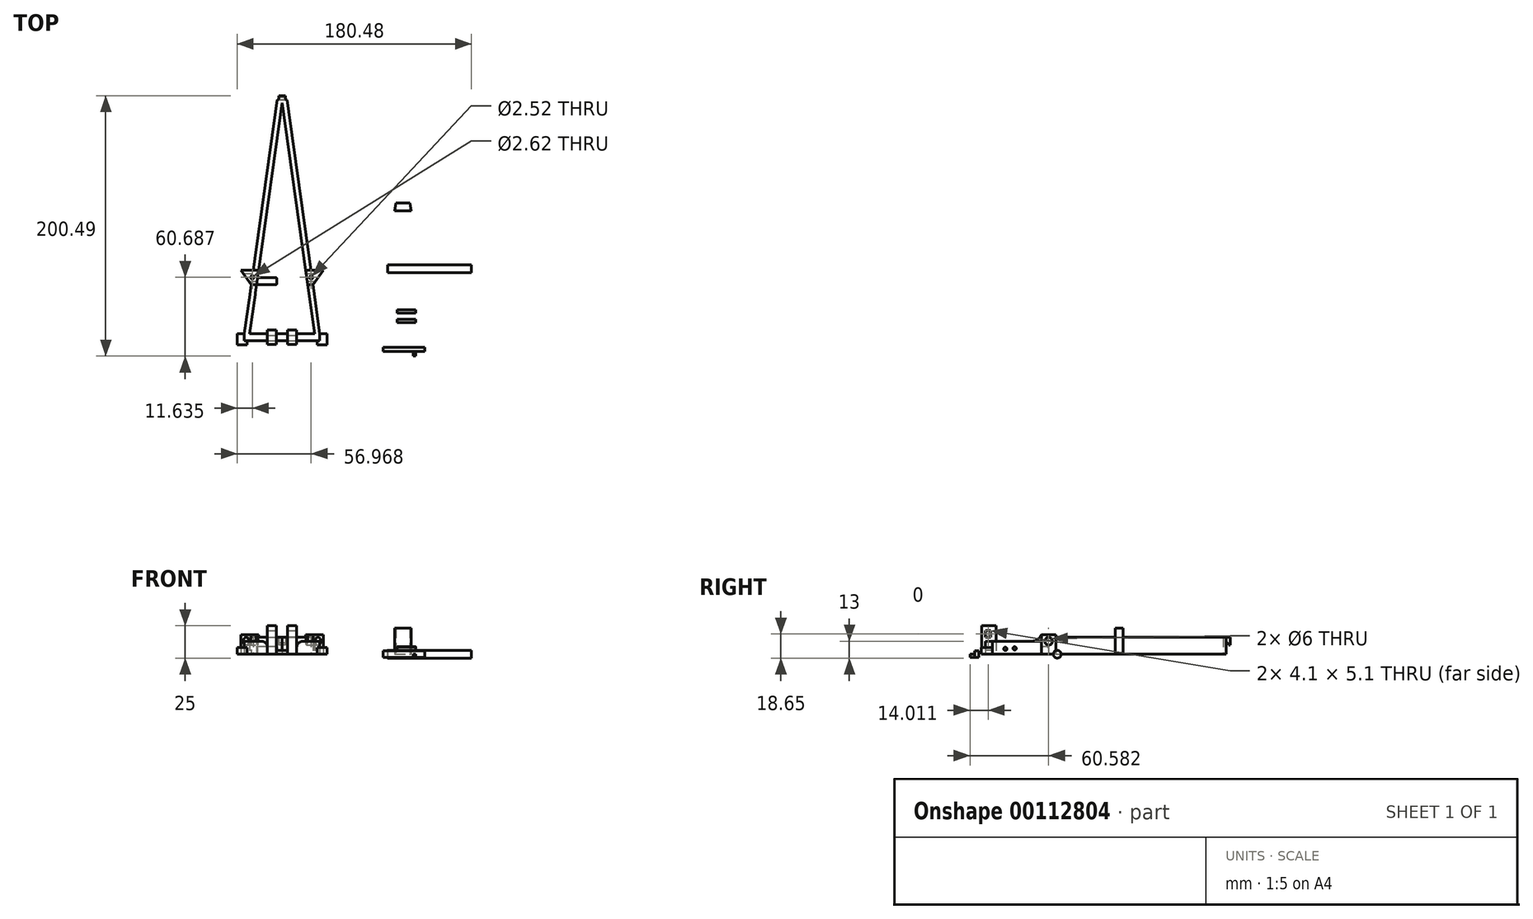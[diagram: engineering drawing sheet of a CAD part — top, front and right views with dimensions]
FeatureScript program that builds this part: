
annotation { "Feature Type Name" : "Feature", "Feature Type Description" : "" }
export const myFeature = defineFeature(function(context is Context, id is Id, definition is map)
    precondition{}
    {
        {
            var Q0;
            Q0=qCreatedBy(makeId("Top.planeOp"),FACE);
            var sketch = newSketch(context, id + "F0", { "sketchPlane" : qUnion([Q0])});
            skLineSegment(sketch, "E0", {"start": v(-127.95, -8.42) * mm, "end": v(-102.95, 169.47) * mm});
            skLineSegment(sketch, "E1", {"start": v(-102.95, 169.47) * mm, "end": v(-77.95, -8.42) * mm});
            skLineSegment(sketch, "E2", {"start": v(-77.95, -8.42) * mm, "end": v(-127.95, -8.42) * mm});
            skLineSegment(sketch, "E3", {"start": v(-131.99, -8.42) * mm, "end": v(-106.66, 171.81) * mm});
            skLineSegment(sketch, "E4", {"start": v(-73.91, -8.42) * mm, "end": v(-99.24, 171.81) * mm});
            skLineSegment(sketch, "E5", {"start": v(-106.66, 171.81) * mm, "end": v(-99.24, 171.81) * mm});
            skLineSegment(sketch, "E6", {"start": v(-107.2, -8.42) * mm, "end": v(-107.2, -13.67) * mm});
            skLineSegment(sketch, "E7", {"start": v(-98.7, -8.42) * mm, "end": v(-98.7, -13.67) * mm});
            skLineSegment(sketch, "E8", {"start": v(-114.2, -8.42) * mm, "end": v(-114.2, -13.67) * mm});
            skLineSegment(sketch, "E9", {"start": v(-91.7, -8.42) * mm, "end": v(-91.7, -13.67) * mm});
            skLineSegment(sketch, "E10", {"start": v(-102.95, 169.47) * mm, "end": v(-102.95, 39.47) * mm, "construction": true});
            skLineSegment(sketch, "E11", {"start": v(-102.95, 39.47) * mm, "end": v(-125.26, 39.47) * mm, "construction": true});
            skLineSegment(sketch, "E12", {"start": v(-102.95, 39.47) * mm, "end": v(-80.64, 39.47) * mm, "construction": true});
            skLineSegment(sketch, "E13", {"start": v(-131.99, -8.42) * mm, "end": v(-131.99, -13.67) * mm});
            skLineSegment(sketch, "E14", {"start": v(-131.99, -13.67) * mm, "end": v(-73.91, -13.67) * mm});
            skLineSegment(sketch, "E15", {"start": v(-73.91, -8.42) * mm, "end": v(-73.91, -13.67) * mm});
            skLineSegment(sketch, "E16", {"start": v(-125.1, 40.59) * mm, "end": v(-134.66, 40.59) * mm});
            skLineSegment(sketch, "E17", {"start": v(-134.66, 40.59) * mm, "end": v(-126.68, 29.34) * mm});
            skLineSegment(sketch, "E18", {"start": v(-80.8, 40.59) * mm, "end": v(-71.24, 40.59) * mm});
            skLineSegment(sketch, "E19", {"start": v(-71.24, 40.59) * mm, "end": v(-79.22, 29.34) * mm});
            skLineSegment(sketch, "E20", {"start": v(-121.06, 40.59) * mm, "end": v(-122.64, 29.34) * mm});
            skLineSegment(sketch, "E21", {"start": v(-122.64, 29.34) * mm, "end": v(-126.68, 29.34) * mm});
            skLineSegment(sketch, "E22", {"start": v(-80.8, 40.59) * mm, "end": v(-84.84, 40.59) * mm});
            skLineSegment(sketch, "E23", {"start": v(-125.1, 40.59) * mm, "end": v(-121.06, 40.59) * mm});
            skLineSegment(sketch, "E24", {"start": v(-102.66, 167.4) * mm, "end": v(-103.24, 167.4) * mm});
            skLineSegment(sketch, "E25", {"start": v(-75.97, -16.98) * mm, "end": v(-68.4, -16.98) * mm});
            skLineSegment(sketch, "E26", {"start": v(-68.4, -16.98) * mm, "end": v(-68.4, -8.42) * mm});
            skLineSegment(sketch, "E27", {"start": v(-68.4, -8.42) * mm, "end": v(-73.91, -8.42) * mm});
            skLineSegment(sketch, "E28", {"start": v(-129.93, -16.98) * mm, "end": v(-137.5, -16.98) * mm});
            skLineSegment(sketch, "E29", {"start": v(-137.5, -16.98) * mm, "end": v(-137.5, -8.42) * mm});
            skLineSegment(sketch, "E30", {"start": v(-137.5, -8.42) * mm, "end": v(-131.99, -8.42) * mm});
            skLineSegment(sketch, "E31", {"start": v(-129.93, -16.98) * mm, "end": v(-129.93, -13.67) * mm});
            skLineSegment(sketch, "E32", {"start": v(-75.97, -16.98) * mm, "end": v(-75.97, -13.67) * mm});
            skLineSegment(sketch, "E33", {"start": v(-84.06, 35.04) * mm, "end": v(-83.26, 29.34) * mm});
            skLineSegment(sketch, "E34", {"start": v(-114.2, -8.42) * mm, "end": v(-114.2, -5.42) * mm});
            skLineSegment(sketch, "E35", {"start": v(-114.2, -5.42) * mm, "end": v(-107.2, -5.42) * mm});
            skLineSegment(sketch, "E36", {"start": v(-107.2, -8.42) * mm, "end": v(-107.2, -5.42) * mm});
            skLineSegment(sketch, "E37", {"start": v(-98.7, -8.42) * mm, "end": v(-98.7, -5.42) * mm});
            skLineSegment(sketch, "E38", {"start": v(-98.7, -5.42) * mm, "end": v(-91.7, -5.42) * mm});
            skLineSegment(sketch, "E39", {"start": v(-91.7, -5.42) * mm, "end": v(-91.7, -8.42) * mm});
            skLineSegment(sketch, "E40", {"start": v(-114.2, -13.67) * mm, "end": v(-114.2, -16.67) * mm});
            skLineSegment(sketch, "E41", {"start": v(-114.2, -16.67) * mm, "end": v(-107.2, -16.67) * mm});
            skLineSegment(sketch, "E42", {"start": v(-107.2, -16.67) * mm, "end": v(-107.2, -13.67) * mm});
            skLineSegment(sketch, "E43", {"start": v(-98.7, -13.67) * mm, "end": v(-98.7, -16.67) * mm});
            skLineSegment(sketch, "E44", {"start": v(-98.7, -16.67) * mm, "end": v(-91.7, -16.67) * mm});
            skLineSegment(sketch, "E45", {"start": v(-91.7, -16.67) * mm, "end": v(-91.7, -13.67) * mm});
            skPoint(sketch, "E46", {"position": v(-102.95, -8.42) * mm});
            skLineSegment(sketch, "E47", {"start": v(-121.85, 34.96) * mm, "end": v(-107, 34.96) * mm});
            skLineSegment(sketch, "E48", {"start": v(-107, 34.96) * mm, "end": v(-107, 29.34) * mm});
            skLineSegment(sketch, "E49", {"start": v(-122.64, 29.34) * mm, "end": v(-121.85, 34.96) * mm});
            skLineSegment(sketch, "E50", {"start": v(-122.64, 29.34) * mm, "end": v(-107, 29.34) * mm});
            skLineSegment(sketch, "E51", {"start": v(-98.9, 35.04) * mm, "end": v(-84.06, 35.04) * mm});
            skLineSegment(sketch, "E52", {"start": v(-98.9, 29.34) * mm, "end": v(-83.26, 29.34) * mm});
            skLineSegment(sketch, "E53", {"start": v(-102.95, 39.47) * mm, "end": v(-102.95, -13.67) * mm, "construction": true});
            skLineSegment(sketch, "E54", {"start": v(-98.9, 35.04) * mm, "end": v(-98.9, 29.34) * mm});
            skLineSegment(sketch, "E55", {"start": v(-83.26, 29.34) * mm, "end": v(-79.22, 29.34) * mm});
            skSolve(sketch);
        }
        {
            var Q0;
            {var subQ1=sQuery(id+"F0.wireOp",EDGE,"IxvvKeQ3-KZ9b-KCKL-WXV7-UOZ3nN7Xo2TJ");var subQ6=sQuery(id+"F0.wireOp",EDGE,"FbiqYw4P-1RQG-BL1q-DGhj-2GP1Vw5vHVuU");var subQ7=makeQuery(id+"F0.imprint","INTERSECT",VERTEX,{"derivedFrom":[subQ6,subQ1]});Q0=makeQuery(id+"F0.imprint","IMPRINT",FACE,{"disambiguationData":[TD([[makeQuery(id+"F0.imprint","IMPRINT",EDGE,{"disambiguationData":[TD([[subQ7,1.0]])],"derivedFrom":subQ6}),1.0]])]});}
            var Q1;
            {var subQ0=sQuery(id+"F0.wireOp",EDGE,"FbiqYw4P-1RQG-BL1q-DGhj-2GP1Vw5vHVuU");var subQ1=sQuery(id+"F0.wireOp",EDGE,"Yzk0jsDl-VeHI-F2jR-thc4-cTdQifIVR2Gs");var subQ2=makeQuery(id+"F0.imprint","INTERSECT",VERTEX,{"derivedFrom":[subQ1,subQ0]});Q1=makeQuery(id+"F0.imprint","IMPRINT",FACE,{"disambiguationData":[TD([[makeQuery(id+"F0.imprint","IMPRINT",EDGE,{"disambiguationData":[TD([[subQ2,1.0]])],"derivedFrom":subQ1}),1.0]])]});}
            var Q2;
            {var subQ10=sQuery(id+"F0.wireOp",EDGE,"KaU3ZsMp-N5BN-qPcV-l7cW-mhWCqVK6BR9j");Q2=makeQuery(id+"F0.imprint","IMPRINT",FACE,{"disambiguationData":[TD([[makeQuery(id+"F0.imprint","IMPRINT",EDGE,{"derivedFrom":subQ10}),-1.0]])]});}
            var Q3;
            {var subQ0=sQuery(id+"F0.wireOp",EDGE,"E5");Q3=makeQuery(id+"F0.imprint","IMPRINT",FACE,{"disambiguationData":[TD([[makeQuery(id+"F0.imprint","IMPRINT",EDGE,{"derivedFrom":subQ0}),-1.0]])]});}
            var Q4;
            {var subQ10=sQuery(id+"F0.wireOp",EDGE,"E2");var subQ12=sQuery(id+"F0.wireOp",EDGE,"E1");var subQ13=makeQuery(id+"F0.imprint","INTERSECT",VERTEX,{"derivedFrom":[subQ12,subQ10]});Q4=makeQuery(id+"F0.imprint","IMPRINT",FACE,{"disambiguationData":[TD([[makeQuery(id+"F0.imprint","IMPRINT",EDGE,{"disambiguationData":[TD([[subQ13,-1.0]])],"derivedFrom":subQ10}),1.0]])]});}
            var Q5;
            {var subQ3=sQuery(id+"F0.wireOp",EDGE,"GJlgNMUq-ztS3-3HpV-WpKS-D9xGor4xouQF");var subQ7=makeQuery(id+"F0.imprint","IMPRINT",VERTEX,{"derivedFrom":subQ3});Q5=makeQuery(id+"F0.imprint","IMPRINT",FACE,{"disambiguationData":[TD([[makeQuery(id+"F0.imprint","IMPRINT",EDGE,{"disambiguationData":[TD([[subQ7,1.0]])],"derivedFrom":subQ3}),1.0]])]});}
            var Q6;
            {var subQ3=sQuery(id+"F0.wireOp",EDGE,"GJlgNMUq-ztS3-3HpV-WpKS-D9xGor4xouQF");var subQ5=makeQuery(id+"F0.imprint","IMPRINT",VERTEX,{"derivedFrom":subQ3});Q6=makeQuery(id+"F0.imprint","IMPRINT",FACE,{"disambiguationData":[TD([[makeQuery(id+"F0.imprint","IMPRINT",EDGE,{"disambiguationData":[TD([[subQ5,1.0]])],"derivedFrom":subQ3}),-1.0]])]});}
            var Q7;
            {var subQ6=sQuery(id+"F0.wireOp",EDGE,"E8");Q7=makeQuery(id+"F0.imprint","IMPRINT",FACE,{"disambiguationData":[TD([[makeQuery(id+"F0.imprint","IMPRINT",EDGE,{"derivedFrom":subQ6}),-1.0]])]});}
            var Q8;
            {var subQ5=sQuery(id+"F0.wireOp",EDGE,"E23");Q8=makeQuery(id+"F0.imprint","IMPRINT",FACE,{"disambiguationData":[TD([[makeQuery(id+"F0.imprint","IMPRINT",EDGE,{"derivedFrom":subQ5}),1.0]])]});}
            var Q9;
            {var subQ5=sQuery(id+"F0.wireOp",EDGE,"E22");Q9=makeQuery(id+"F0.imprint","IMPRINT",FACE,{"disambiguationData":[TD([[makeQuery(id+"F0.imprint","IMPRINT",EDGE,{"derivedFrom":subQ5}),-1.0]])]});}
            var Q10;
            {var subQ3=sQuery(id+"F0.wireOp",EDGE,"E21");Q10=makeQuery(id+"F0.imprint","IMPRINT",FACE,{"disambiguationData":[TD([[makeQuery(id+"F0.imprint","IMPRINT",EDGE,{"derivedFrom":subQ3}),-1.0]])]});}
            var Q11;
            {var subQ1=sQuery(id+"F0.wireOp",EDGE,"E13");Q11=makeQuery(id+"F0.imprint","IMPRINT",FACE,{"disambiguationData":[TD([[makeQuery(id+"F0.imprint","IMPRINT",EDGE,{"derivedFrom":subQ1}),1.0]])]});}
            var Q12;
            {var subQ0=sQuery(id+"F0.wireOp",EDGE,"E15");Q12=makeQuery(id+"F0.imprint","IMPRINT",FACE,{"disambiguationData":[TD([[makeQuery(id+"F0.imprint","IMPRINT",EDGE,{"derivedFrom":subQ0}),-1.0]])]});}
            var Q13;
            {var subQ0=sQuery(id+"F0.wireOp",EDGE,"X4FR0Zau-5dnT-qF32-0aZN-1M90JksqqIT1");var subQ1=sQuery(id+"F0.wireOp",EDGE,"E1");var subQ2=makeQuery(id+"F0.imprint","INTERSECT",VERTEX,{"derivedFrom":[subQ1,subQ0]});Q13=makeQuery(id+"F0.imprint","IMPRINT",FACE,{"disambiguationData":[TD([[makeQuery(id+"F0.imprint","IMPRINT",EDGE,{"disambiguationData":[TD([[subQ2,1.0]])],"derivedFrom":subQ1}),1.0]])]});}
            var Q14;
            {var subQ3=sQuery(id+"F0.wireOp",EDGE,"E18");Q14=makeQuery(id+"F0.imprint","IMPRINT",FACE,{"disambiguationData":[TD([[makeQuery(id+"F0.imprint","IMPRINT",EDGE,{"derivedFrom":subQ3}),-1.0]])]});}
            var Q15;
            {var subQ0=sQuery(id+"F0.wireOp",EDGE,"E22");Q15=makeQuery(id+"F0.imprint","IMPRINT",FACE,{"disambiguationData":[TD([[makeQuery(id+"F0.imprint","IMPRINT",EDGE,{"derivedFrom":subQ0}),1.0]])]});}
            var Q16;
            {var subQ3=sQuery(id+"F0.wireOp",EDGE,"E23");Q16=makeQuery(id+"F0.imprint","IMPRINT",FACE,{"disambiguationData":[TD([[makeQuery(id+"F0.imprint","IMPRINT",EDGE,{"derivedFrom":subQ3}),-1.0]])]});}
            var Q17;
            {var subQ3=sQuery(id+"F0.wireOp",EDGE,"E16");Q17=makeQuery(id+"F0.imprint","IMPRINT",FACE,{"disambiguationData":[TD([[makeQuery(id+"F0.imprint","IMPRINT",EDGE,{"derivedFrom":subQ3}),1.0]])]});}
            extrude(context, id + "F1", {"entities" : qUnion([Q0, Q1, Q2, Q3, Q4, Q5, Q6, Q7, Q8, Q9, Q10, Q11, Q12, Q13, Q14, Q15, Q16, Q17]), "depth" : 10 * mm});
        }
        {
            var Q0;
            Q0=qCreatedBy(makeId("Right.planeOp"),FACE);
            var Q1;
            Q1=sQuery(id+"F0.wireOp",VERTEX,"E1.start");
            cPlane(context, id + "F2", {"entities" : qUnion([Q0, Q1]), "cplaneType" : CPlaneType.PLANE_POINT, "offset" : 25.4 * mm, "width" : 152.4 * mm, "height" : 152.4 * mm});
        }
        {
            var Q0;
            Q0=qCreatedBy(makeId("Top.planeOp"),FACE);
            var sketch = newSketch(context, id + "F3", { "sketchPlane" : qUnion([Q0])});
            skLineSegment(sketch, "E56", {"start": v(-21.78, 41.57) * mm, "end": v(43, 41.57) * mm});
            skLineSegment(sketch, "E57", {"start": v(-25.14, -20.37) * mm, "end": v(7.03, -20.37) * mm});
            skLineSegment(sketch, "E58", {"start": v(0, 8.76) * mm, "end": v(-14.27, 8.76) * mm});
            skLineSegment(sketch, "E59", {"start": v(0, 1.59) * mm, "end": v(-14.27, 1.59) * mm});
            skSolve(sketch);
        }
        {
            var Q0;
            Q0=qCreatedBy(makeId("Right.planeOp"),FACE);
            var sketch = newSketch(context, id + "F4", { "sketchPlane" : qUnion([Q0])});
            skPoint(sketch, "E60.0", {"position": v(41.57, 0) * mm});
            skCircle(sketch, "E61", {"center": v(41.57, 0) * mm, "radius": 3 * mm});
            skPoint(sketch, "E62.0", {"position": v(-20.37, 0) * mm});
            skLineSegment(sketch, "E63.bottom", {"start": v(-21.87, -2.5) * mm, "end": v(-18.87, -2.5) * mm});
            skLineSegment(sketch, "E63.top", {"start": v(-21.87, 2.5) * mm, "end": v(-18.87, 2.5) * mm});
            skLineSegment(sketch, "E63.left", {"start": v(-21.87, -2.5) * mm, "end": v(-21.87, 2.5) * mm});
            skLineSegment(sketch, "E63.right", {"start": v(-18.87, -2.5) * mm, "end": v(-18.87, 2.5) * mm});
            skCircle(sketch, "E64", {"center": v(8.76, 4.47) * mm, "radius": 1.26 * mm});
            skCircle(sketch, "E65", {"center": v(1.59, 4.1) * mm, "radius": 1.26 * mm});
            skLineSegment(sketch, "E66", {"start": v(-21.87, -2.5) * mm, "end": v(-25.62, -2.5) * mm});
            skLineSegment(sketch, "E67", {"start": v(-25.62, -2.5) * mm, "end": v(-25.62, 0) * mm});
            skLineSegment(sketch, "E68", {"start": v(-25.62, 0) * mm, "end": v(-20.37, 0) * mm});
            skSolve(sketch);
        }
        {
            var Q0;
            Q0=makeQuery(id+"F4.imprint","IMPRINT",FACE,{"disambiguationData":[TD([[makeQuery(id+"F4.imprint","IMPRINT",EDGE,{"derivedFrom":sQuery(id+"F4.wireOp",EDGE,"E61")}),1.0]])]});
            var Q1;
            Q1=sQuery(id+"F3.wireOp",EDGE,"E56");
            sweep(context, id + "F5", {"profiles" : qUnion([Q0]), "path" : qUnion([Q1])});
        }
        {
            var Q0;
            {var subQ0=sQuery(id+"F0.wireOp",EDGE,"E6");Q0=makeQuery(id+"F0.imprint","IMPRINT",FACE,{"disambiguationData":[TD([[makeQuery(id+"F0.imprint","IMPRINT",EDGE,{"derivedFrom":subQ0}),-1.0]])]});}
            var Q1;
            {var subQ0=sQuery(id+"F0.wireOp",EDGE,"E7");Q1=makeQuery(id+"F0.imprint","IMPRINT",FACE,{"disambiguationData":[TD([[makeQuery(id+"F0.imprint","IMPRINT",EDGE,{"derivedFrom":subQ0}),1.0]])]});}
            var Q2;
            {var subQ2=sQuery(id+"F0.wireOp",EDGE,"E34");Q2=makeQuery(id+"F0.imprint","IMPRINT",FACE,{"disambiguationData":[TD([[makeQuery(id+"F0.imprint","IMPRINT",EDGE,{"derivedFrom":subQ2}),-1.0]])]});}
            var Q3;
            {var subQ0=sQuery(id+"F0.wireOp",EDGE,"E37");Q3=makeQuery(id+"F0.imprint","IMPRINT",FACE,{"disambiguationData":[TD([[makeQuery(id+"F0.imprint","IMPRINT",EDGE,{"derivedFrom":subQ0}),-1.0]])]});}
            var Q4;
            {var subQ0=sQuery(id+"F0.wireOp",EDGE,"E43");Q4=makeQuery(id+"F0.imprint","IMPRINT",FACE,{"disambiguationData":[TD([[makeQuery(id+"F0.imprint","IMPRINT",EDGE,{"derivedFrom":subQ0}),1.0]])]});}
            var Q5;
            {var subQ2=sQuery(id+"F0.wireOp",EDGE,"E40");Q5=makeQuery(id+"F0.imprint","IMPRINT",FACE,{"disambiguationData":[TD([[makeQuery(id+"F0.imprint","IMPRINT",EDGE,{"derivedFrom":subQ2}),1.0]])]});}
            extrude(context, id + "F6", {"entities" : qUnion([Q0, Q1, Q2, Q3, Q4, Q5]), "depth" : 22 * mm});
        }
        {
            var Q0;
            {var subQ3=sQuery(id+"F0.wireOp",EDGE,"E18");Q0=makeQuery(id+"F0.imprint","IMPRINT",FACE,{"disambiguationData":[TD([[makeQuery(id+"F0.imprint","IMPRINT",EDGE,{"derivedFrom":subQ3}),-1.0]])]});}
            var Q1;
            {var subQ3=sQuery(id+"F0.wireOp",EDGE,"E16");Q1=makeQuery(id+"F0.imprint","IMPRINT",FACE,{"disambiguationData":[TD([[makeQuery(id+"F0.imprint","IMPRINT",EDGE,{"derivedFrom":subQ3}),1.0]])]});}
            var Q2;
            {var subQ3=sQuery(id+"F0.wireOp",EDGE,"E23");Q2=makeQuery(id+"F0.imprint","IMPRINT",FACE,{"disambiguationData":[TD([[makeQuery(id+"F0.imprint","IMPRINT",EDGE,{"derivedFrom":subQ3}),-1.0]])]});}
            var Q3;
            {var subQ3=sQuery(id+"F0.wireOp",EDGE,"E21");Q3=makeQuery(id+"F0.imprint","IMPRINT",FACE,{"disambiguationData":[TD([[makeQuery(id+"F0.imprint","IMPRINT",EDGE,{"derivedFrom":subQ3}),-1.0]])]});}
            var Q4;
            {var subQ0=sQuery(id+"F0.wireOp",EDGE,"E22");Q4=makeQuery(id+"F0.imprint","IMPRINT",FACE,{"disambiguationData":[TD([[makeQuery(id+"F0.imprint","IMPRINT",EDGE,{"derivedFrom":subQ0}),1.0]])]});}
            var Q5;
            {var subQ3=sQuery(id+"F0.wireOp",EDGE,"E33");Q5=makeQuery(id+"F0.imprint","IMPRINT",FACE,{"disambiguationData":[TD([[makeQuery(id+"F0.imprint","IMPRINT",EDGE,{"derivedFrom":subQ3}),1.0]])]});}
            extrude(context, id + "F7", {"entities" : qUnion([Q0, Q1, Q2, Q3, Q4, Q5]), "operationType" : NewBodyOperationType.ADD, "depth" : 15 * mm});
        }
        {
            var Q0;
            Q0=qCreatedBy(makeId("Right.planeOp"),FACE);
            var sketch = newSketch(context, id + "F8", { "sketchPlane" : qUnion([Q0])});
            skLineSegment(sketch, "E69", {"start": v(34.96, 15) * mm, "end": v(34.96, 0) * mm});
            skCircle(sketch, "E70", {"center": v(34.96, 10) * mm, "radius": 3 * mm});
            skSolve(sketch);
        }
        {
            var Q0;
            {var subQ0=sQuery(id+"F8.wireOp",EDGE,"E70");var subQ1=sQuery(id+"F8.wireOp",EDGE,"E69");var subQ2=makeQuery(id+"F8.imprint","INTERSECT",VERTEX,{"disambiguationData":[OD(0.0)],"derivedFrom":[subQ1,subQ0]});Q0=makeQuery(id+"F8.imprint","IMPRINT",FACE,{"disambiguationData":[TD([[makeQuery(id+"F8.imprint","IMPRINT",EDGE,{"disambiguationData":[TD([[subQ2,1.0]])],"derivedFrom":subQ1}),-1.0]])]});}
            var Q1;
            {var subQ0=sQuery(id+"F8.wireOp",EDGE,"E70");var subQ1=sQuery(id+"F8.wireOp",EDGE,"E69");var subQ2=makeQuery(id+"F8.imprint","INTERSECT",VERTEX,{"disambiguationData":[OD(0.0)],"derivedFrom":[subQ1,subQ0]});Q1=makeQuery(id+"F8.imprint","IMPRINT",FACE,{"disambiguationData":[TD([[makeQuery(id+"F8.imprint","IMPRINT",EDGE,{"disambiguationData":[TD([[subQ2,1.0]])],"derivedFrom":subQ1}),1.0]])]});}
            extrude(context, id + "F9", {"entities" : qUnion([Q0, Q1]), "operationType" : NewBodyOperationType.REMOVE, "endBound" : BoundingType.THROUGH_ALL, "oppositeDirection" : true, "depth" : 25.4 * mm});
        }
        {
            var Q0;
            Q0=qCreatedBy(id+"F2.planeOp",FACE);
            var sketch = newSketch(context, id + "F10", { "sketchPlane" : qUnion([Q0])});
            skPoint(sketch, "E71.0", {"position": v(-8.42, 10) * mm});
            skPoint(sketch, "E72.0", {"position": v(169.47, 10) * mm});
            skLineSegment(sketch, "E73", {"start": v(169.47, 10) * mm, "end": v(174.87, 10) * mm});
            skLineSegment(sketch, "E74", {"start": v(174.87, 10) * mm, "end": v(174.87, 7.19) * mm});
            skLineSegment(sketch, "E75", {"start": v(169.47, 10) * mm, "end": v(169.47, 7.19) * mm});
            skLineSegment(sketch, "E76", {"start": v(169.47, 7.19) * mm, "end": v(171.6, 7.19) * mm});
            skArc(sketch, "E77", {"start": v(173.55, 7.19) * mm, "mid": v(171.95, 8.79) * mm, "end": v(170.35, 7.19) * mm});
            skLineSegment(sketch, "E78", {"start": v(173.55, 7.19) * mm, "end": v(174.87, 7.19) * mm});
            skSolve(sketch);
        }
        {
            var Q0;
            Q0=makeQuery(id+"F4.imprint","IMPRINT",FACE,{"disambiguationData":[TD([[makeQuery(id+"F4.imprint","IMPRINT",EDGE,{"derivedFrom":sQuery(id+"F4.wireOp",EDGE,"E63.bottom")}),1.0]])]});
            var Q1;
            Q1=sQuery(id+"F3.wireOp",EDGE,"E57");
            sweep(context, id + "F11", {"profiles" : qUnion([Q0]), "path" : qUnion([Q1])});
        }
        {
            var Q0;
            Q0=makeQuery(id+"F10.imprint","IMPRINT",FACE,{"disambiguationData":[TD([[makeQuery(id+"F10.imprint","IMPRINT",EDGE,{"derivedFrom":sQuery(id+"F10.wireOp",EDGE,"E73")}),-1.0]])]});
            extrude(context, id + "F12", {"entities" : qUnion([Q0]), "operationType" : NewBodyOperationType.ADD, "endBound" : BoundingType.SYMMETRIC, "depth" : 5 * mm});
        }
        {
            var Q0;
            {var subQ1=sQuery(id+"F0.wireOp",EDGE,"E6");Q0=makeQuery(id+"F0.imprint","IMPRINT",FACE,{"disambiguationData":[TD([[makeQuery(id+"F0.imprint","IMPRINT",EDGE,{"derivedFrom":subQ1}),1.0]])]});}
            extrude(context, id + "F13", {"entities" : qUnion([Q0]), "operationType" : NewBodyOperationType.ADD, "depth" : 3 * mm});
        }
        {
            var Q0;
            Q0=makeQuery(id+"F0.imprint","IMPRINT",FACE,{"disambiguationData":[TD([[makeQuery(id+"F0.imprint","IMPRINT",EDGE,{"derivedFrom":sQuery(id+"F0.wireOp",EDGE,"E13")}),-1.0]])]});
            var Q1;
            Q1=makeQuery(id+"F0.imprint","IMPRINT",FACE,{"disambiguationData":[TD([[makeQuery(id+"F0.imprint","IMPRINT",EDGE,{"derivedFrom":sQuery(id+"F0.wireOp",EDGE,"E15")}),1.0]])]});
            var Q2;
            Q2=makeQuery(id+"F1.opExtrude","CAP_FACE",FACE,{"disambiguationData":[OSD([sQuery(id+"F0.wireOp",EDGE,"E0"),sQuery(id+"F0.wireOp",EDGE,"E2"),sQuery(id+"F0.wireOp",EDGE,"E3"),sQuery(id+"F0.wireOp",EDGE,"E8"),sQuery(id+"F0.wireOp",EDGE,"E13"),sQuery(id+"F0.wireOp",EDGE,"E14"),sQuery(id+"F0.wireOp",EDGE,"E21")])],"isStart":false});
            extrude(context, id + "F14", {"entities" : qUnion([Q0, Q1]), "operationType" : NewBodyOperationType.ADD, "endBoundEntityFace" : qUnion([Q2]), "depth" : 5 * mm});
        }
        {
            var Q0;
            Q0=makeQuery(id+"F1.opExtrude","CAP_EDGE",EDGE,{"disambiguationData":[OSD([sQuery(id+"F0.wireOp",EDGE,"E9")])],"isStart":false});
            var Q1;
            Q1=makeQuery(id+"F1.opExtrude","CAP_EDGE",EDGE,{"disambiguationData":[OSD([sQuery(id+"F0.wireOp",EDGE,"E8")])],"isStart":false});
            fillet(context, id + "F15", {"entities" : qUnion([Q0, Q1]), "radius" : 5 * mm, "tangentPropagation" : true, "allowEdgeOverflow" : false});
        }
        {
            var Q0;
            Q0=makeQuery(id+"F0.imprint","IMPRINT",FACE,{"disambiguationData":[TD([[makeQuery(id+"F0.imprint","IMPRINT",EDGE,{"derivedFrom":sQuery(id+"F0.wireOp",EDGE,"E47")}),-1.0]])]});
            var Q1;
            Q1=makeQuery(id+"F0.imprint","IMPRINT",FACE,{"disambiguationData":[TD([[makeQuery(id+"F0.imprint","IMPRINT",EDGE,{"derivedFrom":sQuery(id+"F0.wireOp",EDGE,"E33")}),-1.0]])]});
            extrude(context, id + "F16", {"entities" : qUnion([Q0, Q1]), "operationType" : NewBodyOperationType.ADD, "depth" : 6 * mm});
        }
        {
            var Q0;
            Q0=makeQuery(id+"F12.boolean.opBoolean","INTERSECT",EDGE,{"derivedFrom":[makeQuery(id+"F1.opExtrude","SWEPT_FACE",FACE,{"disambiguationData":[OSD([sQuery(id+"F0.wireOp",EDGE,"E5")])]}),makeQuery(id+"F12.opExtrude","CAP_FACE",FACE,{"disambiguationData":[OSD([sQuery(id+"F10.wireOp",EDGE,"E73"),sQuery(id+"F10.wireOp",EDGE,"E74"),sQuery(id+"F10.wireOp",EDGE,"E75"),sQuery(id+"F10.wireOp",EDGE,"E76"),sQuery(id+"F10.wireOp",EDGE,"E77"),sQuery(id+"F10.wireOp",EDGE,"E78")])],"isStart":false})]});
            var Q1;
            Q1=makeQuery(id+"F12.boolean.opBoolean","INTERSECT",EDGE,{"derivedFrom":[makeQuery(id+"F1.opExtrude","SWEPT_FACE",FACE,{"disambiguationData":[OSD([sQuery(id+"F0.wireOp",EDGE,"E5")])]}),makeQuery(id+"F12.opExtrude","CAP_FACE",FACE,{"disambiguationData":[OSD([sQuery(id+"F10.wireOp",EDGE,"E73"),sQuery(id+"F10.wireOp",EDGE,"E74"),sQuery(id+"F10.wireOp",EDGE,"E75"),sQuery(id+"F10.wireOp",EDGE,"E76"),sQuery(id+"F10.wireOp",EDGE,"E77"),sQuery(id+"F10.wireOp",EDGE,"E78")])],"isStart":true})]});
            fillet(context, id + "F17", {"entities" : qUnion([Q0, Q1]), "radius" : 1 * mm, "tangentPropagation" : true, "allowEdgeOverflow" : false});
        }
        {
            var Q0;
            Q0=makeQuery(id+"F1.opExtrude","SWEPT_FACE",FACE,{"disambiguationData":[OSD([sQuery(id+"F0.wireOp",EDGE,"E15")])]});
            var sketch = newSketch(context, id + "F18", { "sketchPlane" : qUnion([Q0])});
            skLineSegment(sketch, "E79", {"start": v(-13.66, 18.2) * mm, "end": v(-9.56, 18.2) * mm});
            skLineSegment(sketch, "E80", {"start": v(-9.56, 18.2) * mm, "end": v(-9.56, 13.1) * mm});
            skLineSegment(sketch, "E81", {"start": v(-9.56, 13.1) * mm, "end": v(-13.66, 13.1) * mm});
            skLineSegment(sketch, "E82", {"start": v(-13.66, 13.1) * mm, "end": v(-13.66, 18.2) * mm});
            skLineSegment(sketch, "E83.0", {"start": v(-8.42, 0) * mm, "end": v(-13.67, 0) * mm});
            skSolve(sketch);
        }
        {
            var Q0;
            Q0=makeQuery(id+"F18.imprint","IMPRINT",FACE,{"disambiguationData":[TD([[makeQuery(id+"F18.imprint","IMPRINT",EDGE,{"derivedFrom":sQuery(id+"F18.wireOp",EDGE,"E79")}),-1.0]])]});
            extrude(context, id + "F19", {"entities" : qUnion([Q0]), "operationType" : NewBodyOperationType.REMOVE, "endBound" : BoundingType.THROUGH_ALL, "oppositeDirection" : true, "depth" : 25 * mm});
        }
        {
            var Q0;
            {var subQ1=sQuery(id+"F0.wireOp",EDGE,"E16");var subQ2=sQuery(id+"F0.wireOp",EDGE,"E18");var subQ3=sQuery(id+"F0.wireOp",EDGE,"E1");var subQ4=sQuery(id+"F0.wireOp",EDGE,"E5");var subQ7=sQuery(id+"F0.wireOp",EDGE,"E12");var subQ9=sQuery(id+"F0.wireOp",EDGE,"E0");var subQ10=sQuery(id+"F0.wireOp",EDGE,"E3");var subQ11=sQuery(id+"F0.wireOp",EDGE,"E20");var subQ12=sQuery(id+"F0.wireOp",EDGE,"E4");Q0=makeQuery(id+"F12.boolean.opBoolean","MERGE",FACE,{"derivedFrom":[makeQuery(id+"F7.boolean.opBoolean","SPLIT",FACE,{"disambiguationData":[TD([makeQuery(id+"F1.opExtrude","SWEPT_FACE",FACE,{"disambiguationData":[OSD([subQ4])]})])],"derivedFrom":makeQuery(id+"F1.opExtrude","CAP_FACE",FACE,{"disambiguationData":[OSD([subQ9,subQ3,sQuery(id+"F0.wireOp",EDGE,"E2"),subQ10,subQ12,subQ4,sQuery(id+"F0.wireOp",EDGE,"E8"),subQ7,sQuery(id+"F0.wireOp",EDGE,"E13"),sQuery(id+"F0.wireOp",EDGE,"E14"),subQ1,sQuery(id+"F0.wireOp",EDGE,"E17"),subQ2,sQuery(id+"F0.wireOp",EDGE,"E19"),subQ11])],"isStart":false})}),makeQuery(id+"F12.opExtrude","SWEPT_FACE",FACE,{"disambiguationData":[OSD([sQuery(id+"F10.wireOp",EDGE,"E73")])]})]});}
            extrude(context, id + "F20", {"entities" : qUnion([Q0]), "operationType" : NewBodyOperationType.ADD, "depth" : 3 * mm});
        }
        {
            var Q0;
            Q0=makeQuery(id+"F7.boolean.opBoolean","INTERSECT",EDGE,{"derivedFrom":[makeQuery(id+"F1.opExtrude","CAP_FACE",FACE,{"disambiguationData":[OSD([sQuery(id+"F0.wireOp",EDGE,"E0"),sQuery(id+"F0.wireOp",EDGE,"E1"),sQuery(id+"F0.wireOp",EDGE,"E2"),sQuery(id+"F0.wireOp",EDGE,"E3"),sQuery(id+"F0.wireOp",EDGE,"E4"),sQuery(id+"F0.wireOp",EDGE,"E5"),sQuery(id+"F0.wireOp",EDGE,"E8"),sQuery(id+"F0.wireOp",EDGE,"E12"),sQuery(id+"F0.wireOp",EDGE,"E13"),sQuery(id+"F0.wireOp",EDGE,"E14"),sQuery(id+"F0.wireOp",EDGE,"E16"),sQuery(id+"F0.wireOp",EDGE,"E17"),sQuery(id+"F0.wireOp",EDGE,"E18"),sQuery(id+"F0.wireOp",EDGE,"E19"),sQuery(id+"F0.wireOp",EDGE,"E20")])],"isStart":false}),makeQuery(id+"F7.opExtrude","SWEPT_FACE",FACE,{"disambiguationData":[OSD([sQuery(id+"F0.wireOp",EDGE,"E21")])]})]});
            var Q1;
            Q1=makeQuery(id+"F1.opExtrude","CAP_EDGE",EDGE,{"disambiguationData":[OSD([sQuery(id+"F0.wireOp",EDGE,"X4FR0Zau-5dnT-qF32-0aZN-1M90JksqqIT1")])],"isStart":false});
            var Q2;
            Q2=makeQuery(id+"F20.opExtrude","CAP_EDGE",EDGE,{"disambiguationData":[OSD([sQuery(id+"F0.wireOp",EDGE,"E0"),sQuery(id+"F0.wireOp",EDGE,"E1"),sQuery(id+"F0.wireOp",EDGE,"E2"),sQuery(id+"F0.wireOp",EDGE,"E3"),sQuery(id+"F0.wireOp",EDGE,"E4"),sQuery(id+"F0.wireOp",EDGE,"E5"),sQuery(id+"F0.wireOp",EDGE,"E8"),sQuery(id+"F0.wireOp",EDGE,"E12"),sQuery(id+"F0.wireOp",EDGE,"E13"),sQuery(id+"F0.wireOp",EDGE,"E14"),sQuery(id+"F0.wireOp",EDGE,"E16"),sQuery(id+"F0.wireOp",EDGE,"E17"),sQuery(id+"F0.wireOp",EDGE,"E18"),sQuery(id+"F0.wireOp",EDGE,"E19"),sQuery(id+"F0.wireOp",EDGE,"E20"),sQuery(id+"F0.wireOp",EDGE,"E23")])],"isStart":false});
            var Q3;
            Q3=makeQuery(id+"F20.opExtrude","CAP_EDGE",EDGE,{"disambiguationData":[OSD([sQuery(id+"F0.wireOp",EDGE,"E0"),sQuery(id+"F0.wireOp",EDGE,"E1"),sQuery(id+"F0.wireOp",EDGE,"E2"),sQuery(id+"F0.wireOp",EDGE,"E3"),sQuery(id+"F0.wireOp",EDGE,"E4"),sQuery(id+"F0.wireOp",EDGE,"E5"),sQuery(id+"F0.wireOp",EDGE,"E8"),sQuery(id+"F0.wireOp",EDGE,"E12"),sQuery(id+"F0.wireOp",EDGE,"E13"),sQuery(id+"F0.wireOp",EDGE,"E14"),sQuery(id+"F0.wireOp",EDGE,"E16"),sQuery(id+"F0.wireOp",EDGE,"E17"),sQuery(id+"F0.wireOp",EDGE,"E18"),sQuery(id+"F0.wireOp",EDGE,"E19"),sQuery(id+"F0.wireOp",EDGE,"E20"),sQuery(id+"F0.wireOp",EDGE,"E22")])],"isStart":false});
            fillet(context, id + "F21", {"entities" : qUnion([Q0, Q1, Q2, Q3]), "radius" : 8 * mm, "tangentPropagation" : true, "allowEdgeOverflow" : false});
        }
        {
            var Q0;
            Q0=makeQuery(id+"F16.opExtrude","SWEPT_EDGE",EDGE,{"disambiguationData":[OSD([sQuery(id+"F0.wireOp",EDGE,"E50"),sQuery(id+"F0.wireOp",EDGE,"E48")])]});
            var Q1;
            Q1=makeQuery(id+"F16.opExtrude","SWEPT_EDGE",EDGE,{"disambiguationData":[OSD([sQuery(id+"F0.wireOp",EDGE,"E47"),sQuery(id+"F0.wireOp",EDGE,"E48")])]});
            var Q2;
            Q2=makeQuery(id+"F16.opExtrude","SWEPT_EDGE",EDGE,{"disambiguationData":[OSD([sQuery(id+"F0.wireOp",EDGE,"E51"),sQuery(id+"F0.wireOp",EDGE,"E54")])]});
            var Q3;
            Q3=makeQuery(id+"F16.opExtrude","SWEPT_EDGE",EDGE,{"disambiguationData":[OSD([sQuery(id+"F0.wireOp",EDGE,"E52"),sQuery(id+"F0.wireOp",EDGE,"E54")])]});
            var Q4;
            Q4=makeQuery(id+"F16.opExtrude","CAP_EDGE",EDGE,{"disambiguationData":[OSD([sQuery(id+"F0.wireOp",EDGE,"E48")])],"isStart":false});
            var Q5;
            Q5=makeQuery(id+"F16.opExtrude","CAP_EDGE",EDGE,{"disambiguationData":[OSD([sQuery(id+"F0.wireOp",EDGE,"E54")])],"isStart":false});
            fillet(context, id + "F22", {"entities" : qUnion([Q0, Q1, Q2, Q3, Q4, Q5]), "radius" : 1 * mm, "tangentPropagation" : true, "allowEdgeOverflow" : false});
        }
        {
            var Q0;
            Q0=makeQuery(id+"F7.opExtrude","CAP_FACE",FACE,{"disambiguationData":[OSD([sQuery(id+"F0.wireOp",EDGE,"E1"),sQuery(id+"F0.wireOp",EDGE,"E18"),sQuery(id+"F0.wireOp",EDGE,"E19"),sQuery(id+"F0.wireOp",EDGE,"X4FR0Zau-5dnT-qF32-0aZN-1M90JksqqIT1"),sQuery(id+"F0.wireOp",EDGE,"E22"),sQuery(id+"F0.wireOp",EDGE,"E33")])],"isStart":false});
            var sketch = newSketch(context, id + "F23", { "sketchPlane" : qUnion([Q0])});
            skCircle(sketch, "E84", {"center": v(-80.52, 35.07) * mm, "radius": 1.26 * mm});
            skCircle(sketch, "E85", {"center": v(-125.86, 35.07) * mm, "radius": 1.31 * mm});
            skSolve(sketch);
        }
        {
            var Q0;
            Q0=makeQuery(id+"F23.imprint","IMPRINT",FACE,{"disambiguationData":[TD([[makeQuery(id+"F23.imprint","IMPRINT",EDGE,{"derivedFrom":sQuery(id+"F23.wireOp",EDGE,"E85")}),1.0]])]});
            var Q1;
            Q1=makeQuery(id+"F23.imprint","IMPRINT",FACE,{"disambiguationData":[TD([[makeQuery(id+"F23.imprint","IMPRINT",EDGE,{"derivedFrom":sQuery(id+"F23.wireOp",EDGE,"E84")}),1.0]])]});
            extrude(context, id + "F24", {"entities" : qUnion([Q0, Q1]), "operationType" : NewBodyOperationType.REMOVE, "oppositeDirection" : true, "depth" : 5 * mm});
        }
        {
            var Q0;
            Q0=makeQuery(id+"F4.imprint","IMPRINT",FACE,{"disambiguationData":[TD([[makeQuery(id+"F4.imprint","IMPRINT",EDGE,{"derivedFrom":sQuery(id+"F4.wireOp",EDGE,"E64")}),1.0]])]});
            var Q1;
            Q1=makeQuery(id+"F4.imprint","IMPRINT",FACE,{"disambiguationData":[TD([[makeQuery(id+"F4.imprint","IMPRINT",EDGE,{"derivedFrom":sQuery(id+"F4.wireOp",EDGE,"E65")}),1.0]])]});
            var Q2;
            Q2=sQuery(id+"F3.wireOp",EDGE,"E59");
            sweep(context, id + "F25", {"profiles" : qUnion([Q0, Q1]), "path" : qUnion([Q2])});
        }
        {
            var Q0;
            {var subQ8=sQuery(id+"F0.wireOp",EDGE,"E24");Q0=makeQuery(id+"F0.imprint","IMPRINT",FACE,{"disambiguationData":[TD([[makeQuery(id+"F0.imprint","IMPRINT",EDGE,{"derivedFrom":subQ8}),1.0]])]});}
            var sketch = newSketch(context, id + "F26", { "sketchPlane" : qUnion([Q0])});
            skLineSegment(sketch, "E86", {"start": v(-15.32, 92.34) * mm, "end": v(-4.47, 92.34) * mm});
            skLineSegment(sketch, "E87", {"start": v(-16.18, 86.24) * mm, "end": v(-3.61, 86.24) * mm});
            skLineSegment(sketch, "E88", {"start": v(-3.61, 86.24) * mm, "end": v(-4.47, 92.34) * mm});
            skLineSegment(sketch, "E89", {"start": v(-15.32, 92.34) * mm, "end": v(-16.18, 86.24) * mm});
            skSolve(sketch);
        }
        {
            var Q0;
            Q0=makeQuery(id+"F26.imprint","IMPRINT",FACE,{"disambiguationData":[TD([[makeQuery(id+"F26.imprint","IMPRINT",EDGE,{"derivedFrom":sQuery(id+"F26.wireOp",EDGE,"E86")}),-1.0]])]});
            extrude(context, id + "F27", {"entities" : qUnion([Q0]), "operationType" : NewBodyOperationType.ADD, "depth" : 20 * mm});
        }
        {
            var Q0;
            {var subQ0=sQuery(id+"F4.wireOp",EDGE,"E66");Q0=makeQuery(id+"F4.imprint","IMPRINT",FACE,{"disambiguationData":[TD([[makeQuery(id+"F4.imprint","IMPRINT",EDGE,{"derivedFrom":subQ0}),-1.0]])]});}
            extrude(context, id + "F28", {"entities" : qUnion([Q0]), "operationType" : NewBodyOperationType.ADD, "oppositeDirection" : true, "depth" : 2 * mm});
        }
    });
